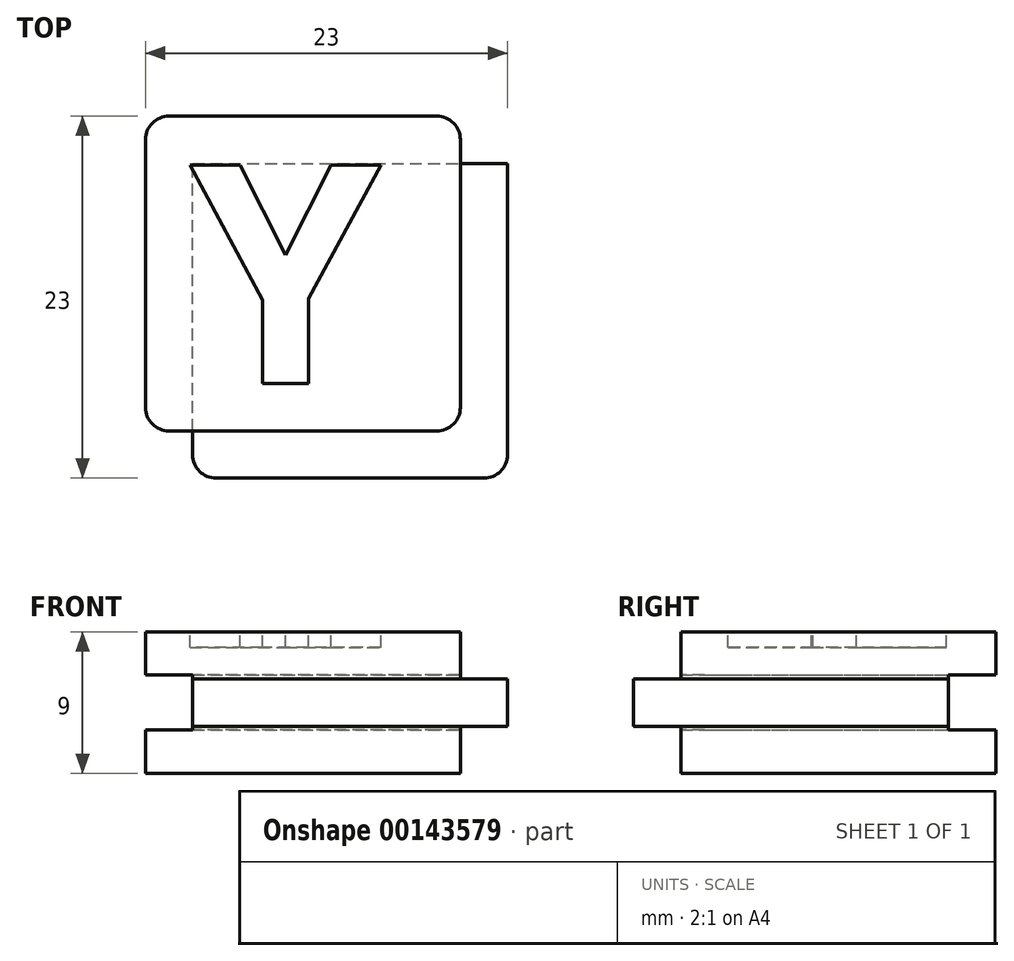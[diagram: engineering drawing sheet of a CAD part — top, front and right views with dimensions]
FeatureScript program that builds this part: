
annotation { "Feature Type Name" : "Feature", "Feature Type Description" : "" }
export const myFeature = defineFeature(function(context is Context, id is Id, definition is map)
    precondition{}
    {
        {
            var Q0;
            Q0=qCreatedBy(makeId("Front.planeOp"),FACE);
            var sketch = newSketch(context, id + "F0", { "sketchPlane" : qUnion([Q0])});
            skLineSegment(sketch, "E0.bottom", {"start": v(10, 4.5) * mm, "end": v(-10, 4.5) * mm});
            skLineSegment(sketch, "E0.top", {"start": v(10, -4.5) * mm, "end": v(-10, -4.5) * mm});
            skLineSegment(sketch, "E0.left", {"start": v(10, 4.5) * mm, "end": v(10, -4.5) * mm});
            skLineSegment(sketch, "E0.right", {"start": v(-10, 4.5) * mm, "end": v(-10, -4.5) * mm});
            skPoint(sketch, "E0.middle", {"position": v(0, 0) * mm});
            skLineSegment(sketch, "E1.bottom", {"start": v(13, 1.5) * mm, "end": v(7, 1.5) * mm});
            skLineSegment(sketch, "E1.top", {"start": v(13, -1.5) * mm, "end": v(7, -1.5) * mm});
            skLineSegment(sketch, "E1.left", {"start": v(13, 1.5) * mm, "end": v(13, -1.5) * mm});
            skLineSegment(sketch, "E1.right", {"start": v(7, 1.5) * mm, "end": v(7, -1.5) * mm});
            skPoint(sketch, "E1.middle", {"position": v(10, 0) * mm});
            skLineSegment(sketch, "E2.bottom", {"start": v(7, 1.5) * mm, "end": v(-7, 1.5) * mm});
            skLineSegment(sketch, "E2.top", {"start": v(7, -1.5) * mm, "end": v(-7, -1.5) * mm});
            skLineSegment(sketch, "E2.right", {"start": v(-7, 1.5) * mm, "end": v(-7, -1.5) * mm});
            skLineSegment(sketch, "E3.bottom", {"start": v(-7, -1.5) * mm, "end": v(-10, -1.5) * mm});
            skLineSegment(sketch, "E3.top", {"start": v(-7, 1.5) * mm, "end": v(-10, 1.5) * mm});
            skLineSegment(sketch, "E3.left", {"start": v(-7, -1.5) * mm, "end": v(-7, 1.5) * mm});
            skLineSegment(sketch, "E3.right", {"start": v(-10, -1.5) * mm, "end": v(-10, 1.5) * mm});
            skSolve(sketch);
        }
        {
            var Q0;
            {var subQ5=sQuery(id+"F0.wireOp",EDGE,"E0.bottom");Q0=makeQuery(id+"F0.imprint","IMPRINT",FACE,{"disambiguationData":[TD([[makeQuery(id+"F0.imprint","IMPRINT",EDGE,{"derivedFrom":subQ5}),1.0]])]});}
            var Q1;
            Q1=makeQuery(id+"F0.imprint","IMPRINT",FACE,{"disambiguationData":[TD([[makeQuery(id+"F0.imprint","IMPRINT",EDGE,{"derivedFrom":sQuery(id+"F0.wireOp",EDGE,"E2.bottom")}),1.0]])]});
            var Q2;
            {var subQ5=sQuery(id+"F0.wireOp",EDGE,"E1.left");Q2=makeQuery(id+"F0.imprint","IMPRINT",FACE,{"disambiguationData":[TD([[makeQuery(id+"F0.imprint","IMPRINT",EDGE,{"derivedFrom":subQ5}),-1.0]])]});}
            var Q3;
            {var subQ5=sQuery(id+"F0.wireOp",EDGE,"E1.right");Q3=makeQuery(id+"F0.imprint","IMPRINT",FACE,{"disambiguationData":[TD([[makeQuery(id+"F0.imprint","IMPRINT",EDGE,{"derivedFrom":subQ5}),1.0]])]});}
            var Q4;
            Q4=makeQuery(id+"F0.imprint","IMPRINT",FACE,{"disambiguationData":[TD([[makeQuery(id+"F0.imprint","IMPRINT",EDGE,{"derivedFrom":sQuery(id+"F0.wireOp",EDGE,"E3.bottom")}),-1.0]])]});
            var Q5;
            {var subQ5=sQuery(id+"F0.wireOp",EDGE,"E0.top");Q5=makeQuery(id+"F0.imprint","IMPRINT",FACE,{"disambiguationData":[TD([[makeQuery(id+"F0.imprint","IMPRINT",EDGE,{"derivedFrom":subQ5}),-1.0]])]});}
            extrude(context, id + "F1", {"entities" : qUnion([Q0, Q1, Q2, Q3, Q4, Q5]), "oppositeDirection" : true, "depth" : 20 * mm});
        }
        {
            var Q0;
            Q0=makeQuery(id+"F0.imprint","IMPRINT",FACE,{"disambiguationData":[TD([[makeQuery(id+"F0.imprint","IMPRINT",EDGE,{"derivedFrom":sQuery(id+"F0.wireOp",EDGE,"E3.bottom")}),-1.0]])]});
            var Q1;
            Q1=makeQuery(id+"F0.imprint","IMPRINT",FACE,{"disambiguationData":[TD([[makeQuery(id+"F0.imprint","IMPRINT",EDGE,{"derivedFrom":sQuery(id+"F0.wireOp",EDGE,"E2.bottom")}),1.0]])]});
            var Q2;
            {var subQ5=sQuery(id+"F0.wireOp",EDGE,"E1.right");Q2=makeQuery(id+"F0.imprint","IMPRINT",FACE,{"disambiguationData":[TD([[makeQuery(id+"F0.imprint","IMPRINT",EDGE,{"derivedFrom":subQ5}),1.0]])]});}
            var Q3;
            {var subQ5=sQuery(id+"F0.wireOp",EDGE,"E1.left");Q3=makeQuery(id+"F0.imprint","IMPRINT",FACE,{"disambiguationData":[TD([[makeQuery(id+"F0.imprint","IMPRINT",EDGE,{"derivedFrom":subQ5}),-1.0]])]});}
            extrude(context, id + "F2", {"entities" : qUnion([Q0, Q1, Q2, Q3]), "operationType" : NewBodyOperationType.ADD, "depth" : 3 * mm});
        }
        {
            var Q0;
            {var subQ0=sQuery(id+"F0.wireOp",EDGE,"E1.left");Q0=makeQuery(id+"F2.boolean.opBoolean","MERGE",FACE,{"derivedFrom":[makeQuery(id+"F1.opExtrude","SWEPT_FACE",FACE,{"disambiguationData":[OSD([subQ0])]}),makeQuery(id+"F2.opExtrude","SWEPT_FACE",FACE,{"disambiguationData":[OSD([subQ0])]})]});}
            var sketch = newSketch(context, id + "F3", { "sketchPlane" : qUnion([Q0])});
            skLineSegment(sketch, "E4.bottom", {"start": v(23, 1.75) * mm, "end": v(17, 1.75) * mm});
            skLineSegment(sketch, "E4.top", {"start": v(23, -1.75) * mm, "end": v(17, -1.75) * mm});
            skLineSegment(sketch, "E4.left", {"start": v(23, 1.75) * mm, "end": v(23, -1.75) * mm});
            skLineSegment(sketch, "E4.right", {"start": v(17, 1.75) * mm, "end": v(17, -1.75) * mm});
            skPoint(sketch, "E4.middle", {"position": v(20, 0) * mm});
            skSolve(sketch);
        }
        {
            var Q0;
            {var subQ1=sQuery(id+"F3.wireOp",EDGE,"E4.bottom");Q0=makeQuery(id+"F3.imprint","IMPRINT",FACE,{"disambiguationData":[TD([[makeQuery(id+"F3.imprint","IMPRINT",EDGE,{"derivedFrom":subQ1}),1.0]])]});}
            var Q1;
            {var subQ1=sQuery(id+"F0.wireOp",EDGE,"E1.left");var subQ8=makeQuery(id+"F1.opExtrude","CAP_EDGE",EDGE,{"disambiguationData":[OSD([subQ1])],"isStart":false});Q1=makeQuery(id+"F3.imprint","IMPRINT",FACE,{"disambiguationData":[TD([[makeQuery(id+"F3.imprint","IMPRINT",EDGE,{"derivedFrom":subQ8}),-1.0]])]});}
            extrude(context, id + "F4", {"entities" : qUnion([Q0, Q1]), "operationType" : NewBodyOperationType.REMOVE, "oppositeDirection" : true, "depth" : 100 * mm});
        }
        {
            var Q0;
            Q0=makeQuery(id+"F4.boolean.opBoolean","COPY",FACE,{"derivedFrom":makeQuery(id+"F4.opExtrude","SWEPT_FACE",FACE,{"disambiguationData":[OSD([sQuery(id+"F3.wireOp",EDGE,"E4.right")])]})});
            var sketch = newSketch(context, id + "F5", { "sketchPlane" : qUnion([Q0])});
            skLineSegment(sketch, "E5.bottom", {"start": v(13, 1.75) * mm, "end": v(7, 1.75) * mm});
            skLineSegment(sketch, "E5.top", {"start": v(13, -1.75) * mm, "end": v(7, -1.75) * mm});
            skLineSegment(sketch, "E5.left", {"start": v(13, 1.75) * mm, "end": v(13, -1.75) * mm});
            skLineSegment(sketch, "E5.right", {"start": v(7, 1.75) * mm, "end": v(7, -1.75) * mm});
            skPoint(sketch, "E5.middle", {"position": v(10, 0) * mm});
            skSolve(sketch);
        }
        {
            var Q0;
            {var subQ3=sQuery(id+"F5.wireOp",EDGE,"E5.left");Q0=makeQuery(id+"F5.imprint","IMPRINT",FACE,{"disambiguationData":[TD([[makeQuery(id+"F5.imprint","IMPRINT",EDGE,{"derivedFrom":subQ3}),-1.0]])]});}
            var Q1;
            {var subQ4=sQuery(id+"F5.wireOp",EDGE,"E5.right");Q1=makeQuery(id+"F5.imprint","IMPRINT",FACE,{"disambiguationData":[TD([[makeQuery(id+"F5.imprint","IMPRINT",EDGE,{"derivedFrom":subQ4}),1.0]])]});}
            extrude(context, id + "F6", {"entities" : qUnion([Q0, Q1]), "operationType" : NewBodyOperationType.REMOVE, "oppositeDirection" : true, "depth" : 100 * mm});
        }
        {
            var Q0;
            Q0=makeQuery(id+"F6.boolean.opBoolean","INTERSECT",EDGE,{"derivedFrom":[makeQuery(id+"F2.opExtrude","CAP_FACE",FACE,{"disambiguationData":[OSD([sQuery(id+"F0.wireOp",EDGE,"E1.bottom"),sQuery(id+"F0.wireOp",EDGE,"E1.top"),sQuery(id+"F0.wireOp",EDGE,"E1.left"),sQuery(id+"F0.wireOp",EDGE,"E2.bottom"),sQuery(id+"F0.wireOp",EDGE,"E2.top"),sQuery(id+"F0.wireOp",EDGE,"E3.bottom"),sQuery(id+"F0.wireOp",EDGE,"E3.top"),sQuery(id+"F0.wireOp",EDGE,"E3.right")])],"isStart":false}),makeQuery(id+"F6.opExtrude","SWEPT_FACE",FACE,{"disambiguationData":[OSD([sQuery(id+"F5.wireOp",EDGE,"E5.right")])]})]});
            var Q1;
            Q1=makeQuery(id+"F2.opExtrude","CAP_EDGE",EDGE,{"disambiguationData":[OSD([sQuery(id+"F0.wireOp",EDGE,"E1.left")])],"isStart":false});
            var Q2;
            {var subQ0=sQuery(id+"F0.wireOp",EDGE,"E0.left");Q2=makeQuery(id+"F1.opExtrude","CAP_EDGE",EDGE,{"disambiguationData":[OSD([subQ0]),TDD([makeQuery(id+"F0.imprint","IMPRINT",EDGE,{"disambiguationData":[TD([[makeQuery(id+"F0.imprint","INTERSECT",VERTEX,{"derivedFrom":[sQuery(id+"F0.wireOp",EDGE,"E0.bottom"),subQ0]}),-1.0]])],"derivedFrom":subQ0})])],"isStart":true});}
            var Q3;
            {var subQ0=sQuery(id+"F0.wireOp",EDGE,"E0.left");Q3=makeQuery(id+"F1.opExtrude","CAP_EDGE",EDGE,{"disambiguationData":[OSD([subQ0]),TDD([makeQuery(id+"F0.imprint","IMPRINT",EDGE,{"disambiguationData":[TD([[makeQuery(id+"F0.imprint","INTERSECT",VERTEX,{"derivedFrom":[sQuery(id+"F0.wireOp",EDGE,"E0.top"),subQ0]}),1.0]])],"derivedFrom":subQ0})])],"isStart":true});}
            var Q4;
            {var subQ0=sQuery(id+"F0.wireOp",EDGE,"E3.right");var subQ1=sQuery(id+"F0.wireOp",EDGE,"E0.right");var subQ3=sQuery(id+"F0.wireOp",EDGE,"E0.top");Q4=makeQuery(id+"F2.boolean.opBoolean","SPLIT",EDGE,{"disambiguationData":[TD([makeQuery(id+"F1.opExtrude","SWEPT_FACE",FACE,{"disambiguationData":[OSD([subQ3])]})])],"derivedFrom":makeQuery(id+"F1.opExtrude","CAP_EDGE",EDGE,{"disambiguationData":[OSD([subQ1,subQ0])],"isStart":true})});}
            var Q5;
            {var subQ1=sQuery(id+"F0.wireOp",EDGE,"E3.right");var subQ2=sQuery(id+"F0.wireOp",EDGE,"E0.right");var subQ3=sQuery(id+"F0.wireOp",EDGE,"E0.bottom");Q5=makeQuery(id+"F2.boolean.opBoolean","SPLIT",EDGE,{"disambiguationData":[TD([makeQuery(id+"F1.opExtrude","SWEPT_FACE",FACE,{"disambiguationData":[OSD([subQ3])]})])],"derivedFrom":makeQuery(id+"F1.opExtrude","CAP_EDGE",EDGE,{"disambiguationData":[OSD([subQ2,subQ1])],"isStart":true})});}
            var Q6;
            Q6=makeQuery(id+"F6.boolean.opBoolean","COPY",EDGE,{"derivedFrom":makeQuery(id+"F6.opExtrude","CAP_EDGE",EDGE,{"disambiguationData":[OSD([sQuery(id+"F5.wireOp",EDGE,"E5.right")])],"isStart":true})});
            var Q7;
            {var subQ0=sQuery(id+"F0.wireOp",EDGE,"E3.right");var subQ1=sQuery(id+"F0.wireOp",EDGE,"E0.right");var subQ2=sQuery(id+"F0.wireOp",EDGE,"E0.bottom");Q7=makeQuery(id+"F4.boolean.opBoolean","SPLIT",EDGE,{"disambiguationData":[TD([makeQuery(id+"F1.opExtrude","SWEPT_FACE",FACE,{"disambiguationData":[OSD([subQ2])]})])],"derivedFrom":makeQuery(id+"F1.opExtrude","CAP_EDGE",EDGE,{"disambiguationData":[OSD([subQ1,subQ0])],"isStart":false})});}
            var Q8;
            {var subQ0=sQuery(id+"F0.wireOp",EDGE,"E3.right");var subQ1=sQuery(id+"F0.wireOp",EDGE,"E0.right");var subQ2=sQuery(id+"F0.wireOp",EDGE,"E0.top");Q8=makeQuery(id+"F4.boolean.opBoolean","SPLIT",EDGE,{"disambiguationData":[TD([makeQuery(id+"F1.opExtrude","SWEPT_FACE",FACE,{"disambiguationData":[OSD([subQ2])]})])],"derivedFrom":makeQuery(id+"F1.opExtrude","CAP_EDGE",EDGE,{"disambiguationData":[OSD([subQ1,subQ0])],"isStart":false})});}
            var Q9;
            Q9=makeQuery(id+"F4.boolean.opBoolean","COPY",EDGE,{"derivedFrom":makeQuery(id+"F4.opExtrude","CAP_EDGE",EDGE,{"disambiguationData":[OSD([sQuery(id+"F3.wireOp",EDGE,"E4.right")])],"isStart":true})});
            var Q10;
            {var subQ0=sQuery(id+"F0.wireOp",EDGE,"E0.left");Q10=makeQuery(id+"F1.opExtrude","CAP_EDGE",EDGE,{"disambiguationData":[OSD([subQ0]),TDD([makeQuery(id+"F0.imprint","IMPRINT",EDGE,{"disambiguationData":[TD([[makeQuery(id+"F0.imprint","INTERSECT",VERTEX,{"derivedFrom":[sQuery(id+"F0.wireOp",EDGE,"E0.bottom"),subQ0]}),-1.0]])],"derivedFrom":subQ0})])],"isStart":false});}
            var Q11;
            {var subQ0=sQuery(id+"F0.wireOp",EDGE,"E0.left");Q11=makeQuery(id+"F1.opExtrude","CAP_EDGE",EDGE,{"disambiguationData":[OSD([subQ0]),TDD([makeQuery(id+"F0.imprint","IMPRINT",EDGE,{"disambiguationData":[TD([[makeQuery(id+"F0.imprint","INTERSECT",VERTEX,{"derivedFrom":[sQuery(id+"F0.wireOp",EDGE,"E0.top"),subQ0]}),1.0]])],"derivedFrom":subQ0})])],"isStart":false});}
            fillet(context, id + "F7", {"entities" : qUnion([Q0, Q1, Q2, Q3, Q4, Q5, Q6, Q7, Q8, Q9, Q10, Q11]), "radius" : 1.5 * mm, "tangentPropagation" : true, "allowEdgeOverflow" : false});
        }
        {
            var Q0;
            Q0=makeQuery(id+"F1.opExtrude","SWEPT_FACE",FACE,{"disambiguationData":[OSD([sQuery(id+"F0.wireOp",EDGE,"E0.bottom")])]});
            var sketch = newSketch(context, id + "F8", { "sketchPlane" : qUnion([Q0])});
            skText(sketch, "E6", { "text": "Y", "fontName": "OpenSans-Bold.ttf"});
            skLineSegment(sketch, "E7.0", {"start": v(9.63, 3) * mm, "end": v(-10.6, 3) * mm});
            const initialGuessF8  = {"E6": [-0.00718, 0.003, 1, 0, 0.014]};
            skSetInitialGuess(sketch, initialGuessF8);
            skSolve(sketch);
        }
        {
            var Q0;
            Q0=makeQuery(id+"F8.imprint","IMPRINT",FACE,{"disambiguationData":[TD([[makeQuery(id+"F8.imprint","IMPRINT",EDGE,{"derivedFrom":sQuery(id+"F8.wireOp",EDGE,"E6.sketch_text.stroke-0")}),-1.0]])]});
            extrude(context, id + "F9", {"entities" : qUnion([Q0]), "operationType" : NewBodyOperationType.REMOVE, "oppositeDirection" : true, "depth" : 1 * mm});
        }
    });
